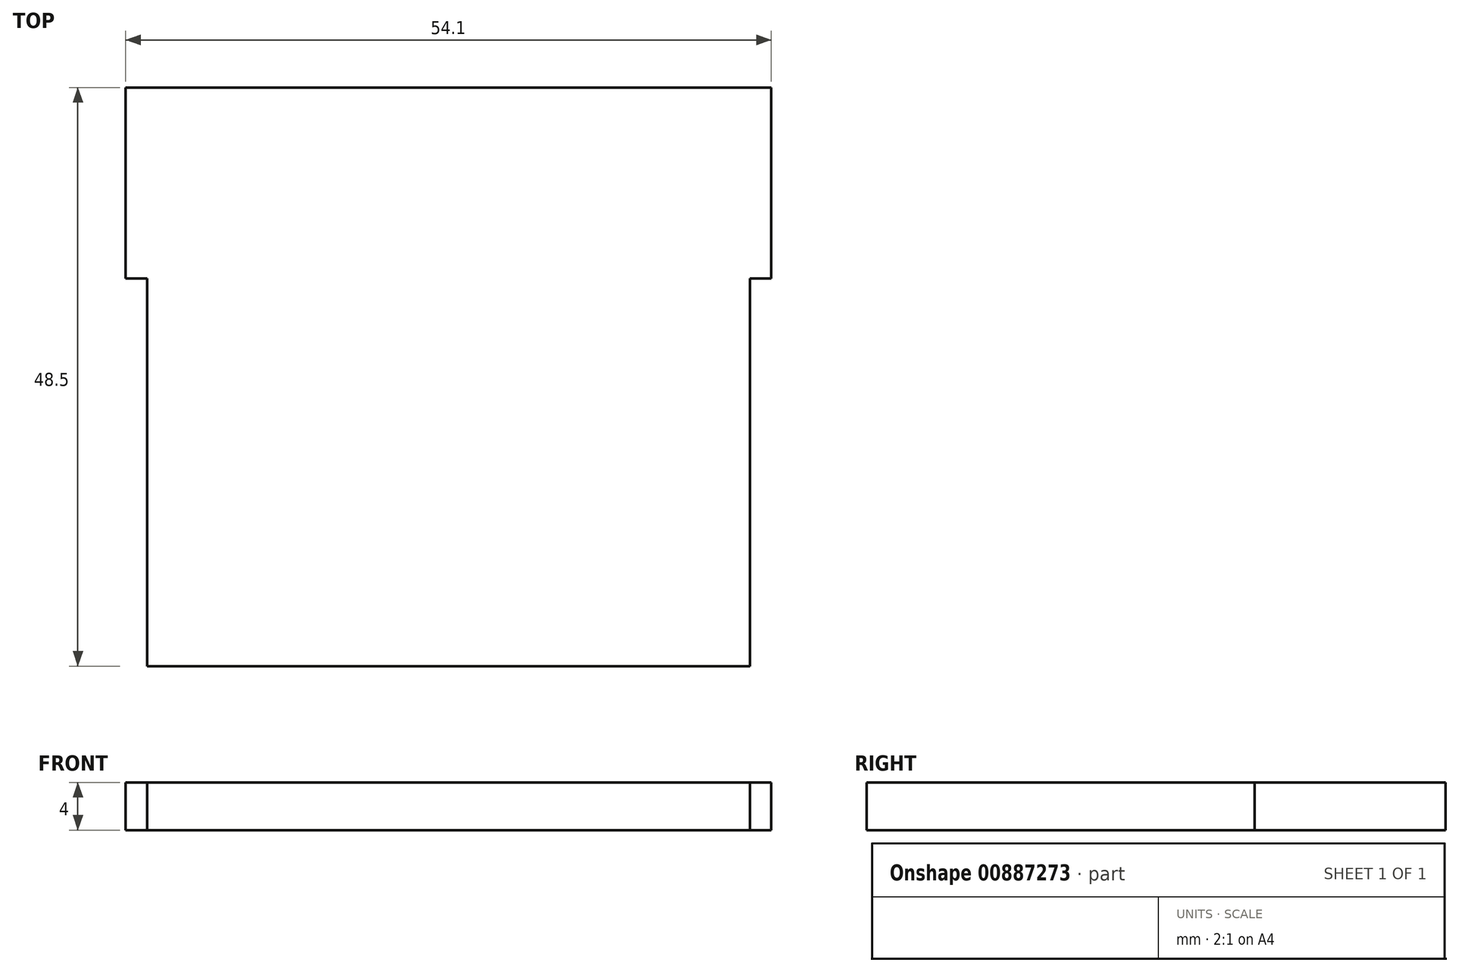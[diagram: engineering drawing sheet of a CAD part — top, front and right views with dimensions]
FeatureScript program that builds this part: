
annotation { "Feature Type Name" : "Feature", "Feature Type Description" : "" }
export const myFeature = defineFeature(function(context is Context, id is Id, definition is map)
    precondition{}
    {
        {
            var Q0;
            Q0=qCreatedBy(makeId("Top.planeOp"),FACE);
            var sketch = newSketch(context, id + "F0", { "sketchPlane" : qUnion([Q0])});
            skLineSegment(sketch, "E0.bottom", {"start": v(23.25, -14.25) * mm, "end": v(-23.25, -14.25) * mm, "construction": true});
            skLineSegment(sketch, "E0.top", {"start": v(23.25, 14.25) * mm, "end": v(-23.25, 14.25) * mm, "construction": true});
            skLineSegment(sketch, "E0.left", {"start": v(23.25, -14.25) * mm, "end": v(23.25, 14.25) * mm, "construction": true});
            skLineSegment(sketch, "E0.right", {"start": v(-23.25, -14.25) * mm, "end": v(-23.25, 14.25) * mm, "construction": true});
            skPoint(sketch, "E0.middle", {"position": v(0, 0) * mm});
            skLineSegment(sketch, "E1.bottom", {"start": v(25.25, -16.25) * mm, "end": v(-25.25, -16.25) * mm});
            skLineSegment(sketch, "E1.left", {"start": v(25.25, -16.25) * mm, "end": v(25.25, 16.25) * mm});
            skLineSegment(sketch, "E1.right", {"start": v(-25.25, -16.25) * mm, "end": v(-25.25, 16.25) * mm});
            skLineSegment(sketch, "E2.bottom", {"start": v(-27.05, 16.25) * mm, "end": v(-25.25, 16.25) * mm});
            skLineSegment(sketch, "E2.top", {"start": v(-27.05, 32.25) * mm, "end": v(27.05, 32.25) * mm});
            skLineSegment(sketch, "E2.left", {"start": v(-27.05, 16.25) * mm, "end": v(-27.05, 32.25) * mm});
            skLineSegment(sketch, "E2.right", {"start": v(27.05, 16.25) * mm, "end": v(27.05, 32.25) * mm});
            skLineSegment(sketch, "E3", {"start": v(-19.05, 24.25) * mm, "end": v(-9.78, 24.25) * mm, "construction": true});
            skLineSegment(sketch, "E4", {"start": v(-9.78, 24.25) * mm, "end": v(0, 24.25) * mm, "construction": true});
            skLineSegment(sketch, "E5", {"start": v(0, 24.25) * mm, "end": v(9.78, 24.25) * mm, "construction": true});
            skLineSegment(sketch, "E6", {"start": v(9.78, 24.25) * mm, "end": v(19.05, 24.25) * mm, "construction": true});
            skLineSegment(sketch, "E7.trimOffspring", {"start": v(25.25, 16.25) * mm, "end": v(27.05, 16.25) * mm});
            skLineSegment(sketch, "E8", {"start": v(-28.58, 0) * mm, "end": v(28.58, 0) * mm, "construction": true});
            skLineSegment(sketch, "E9.bottom", {"start": v(-25.25, -3.33) * mm, "end": v(-31.9, -3.33) * mm});
            skLineSegment(sketch, "E9.top", {"start": v(-25.25, 3.33) * mm, "end": v(-31.9, 3.33) * mm});
            skLineSegment(sketch, "E9.left", {"start": v(-25.25, -3.33) * mm, "end": v(-25.25, 3.33) * mm});
            skLineSegment(sketch, "E9.right", {"start": v(-31.9, -3.33) * mm, "end": v(-31.9, 3.33) * mm});
            skPoint(sketch, "E9.middle", {"position": v(-28.58, 0) * mm});
            skLineSegment(sketch, "E10.bottom", {"start": v(25.25, -3.32) * mm, "end": v(31.9, -3.32) * mm});
            skLineSegment(sketch, "E10.top", {"start": v(25.25, 3.33) * mm, "end": v(31.9, 3.33) * mm});
            skLineSegment(sketch, "E10.left", {"start": v(25.25, -3.32) * mm, "end": v(25.25, 3.33) * mm});
            skLineSegment(sketch, "E10.right", {"start": v(31.9, -3.32) * mm, "end": v(31.9, 3.33) * mm});
            skPoint(sketch, "E10.middle", {"position": v(28.58, 0) * mm});
            skSolve(sketch);
        }
        {
            var Q0;
            Q0=makeQuery(id+"F0.imprint","IMPRINT",FACE,{"disambiguationData":[TD([[makeQuery(id+"F0.imprint","IMPRINT",EDGE,{"derivedFrom":sQuery(id+"F0.wireOp",EDGE,"E1.bottom")}),-1.0]])]});
            extrude(context, id + "F1", {"entities" : qUnion([Q0]), "depth" : 4 * mm, "offsetDistance" : 25 * mm});
        }
    });
